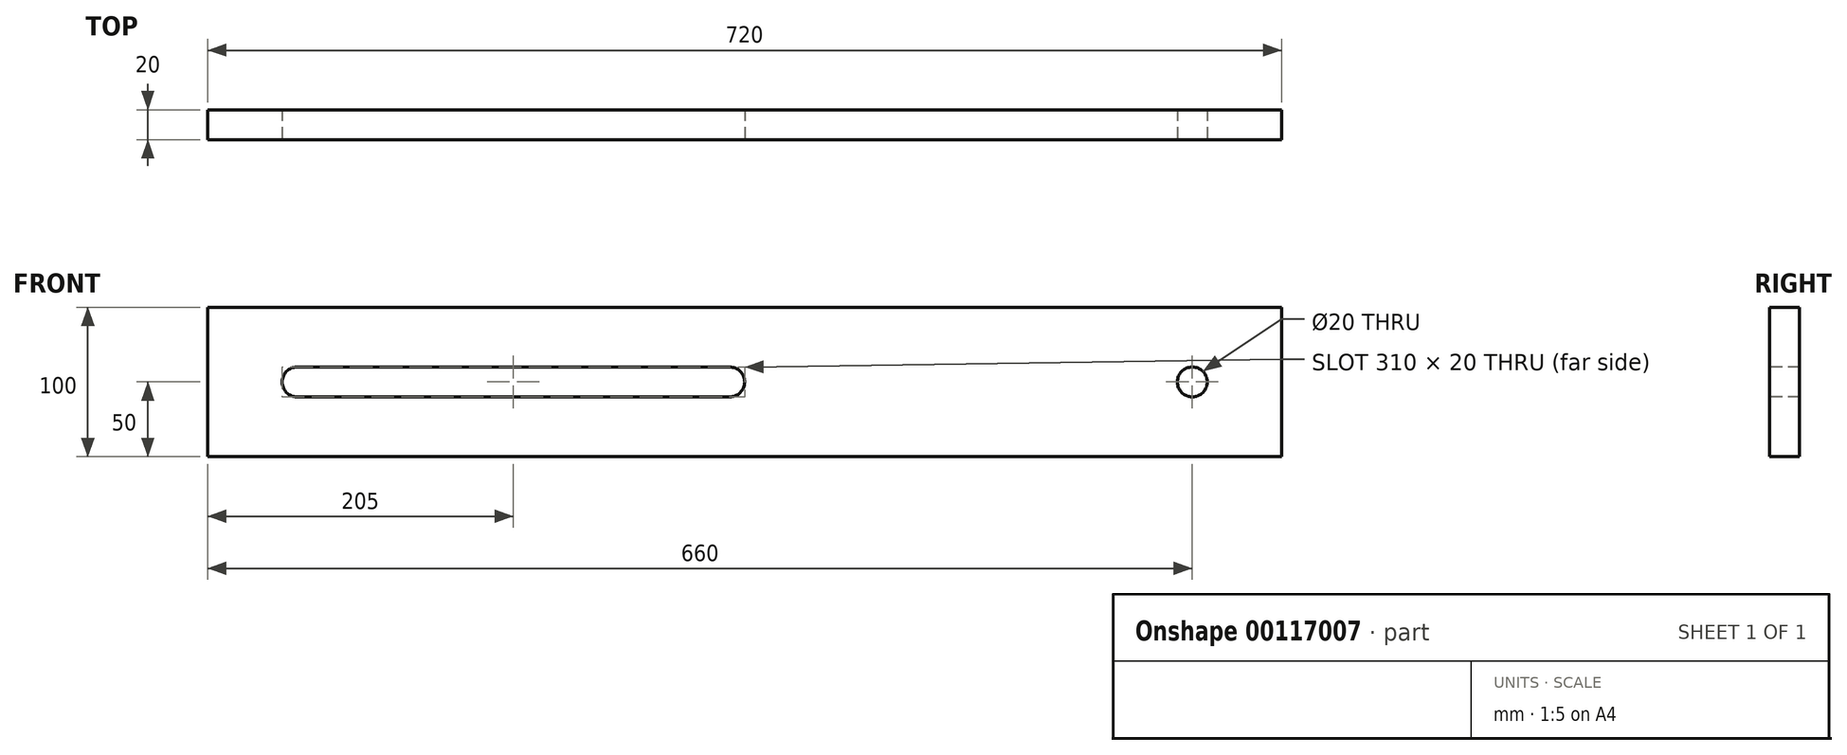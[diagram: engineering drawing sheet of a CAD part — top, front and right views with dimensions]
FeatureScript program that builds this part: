
annotation { "Feature Type Name" : "Feature", "Feature Type Description" : "" }
export const myFeature = defineFeature(function(context is Context, id is Id, definition is map)
    precondition{}
    {
        {
            var Q0;
            Q0=qCreatedBy(makeId("Top.planeOp"),FACE);
            var sketch = newSketch(context, id + "F0", { "sketchPlane" : qUnion([Q0])});
            skLineSegment(sketch, "E0.bottom", {"start": v(-359.02, 161.63) * mm, "end": v(360.98, 161.63) * mm});
            skLineSegment(sketch, "E0.top", {"start": v(-359.02, 141.63) * mm, "end": v(360.98, 141.63) * mm});
            skLineSegment(sketch, "E0.left", {"start": v(-359.02, 161.63) * mm, "end": v(-359.02, 141.63) * mm});
            skLineSegment(sketch, "E0.right", {"start": v(360.98, 161.63) * mm, "end": v(360.98, 141.63) * mm});
            skSolve(sketch);
        }
        {
            var Q0;
            Q0=makeQuery(id+"F0.imprint","IMPRINT",FACE,{"disambiguationData":[TD([[makeQuery(id+"F0.imprint","IMPRINT",EDGE,{"derivedFrom":sQuery(id+"F0.wireOp",EDGE,"E0.bottom")}),-1.0]])]});
            extrude(context, id + "F1", {"entities" : qUnion([Q0]), "depth" : 100 * mm, "offsetDistance" : 25 * mm});
        }
        {
            var Q0;
            Q0=makeQuery(id+"F1.opExtrude","SWEPT_FACE",FACE,{"disambiguationData":[OSD([sQuery(id+"F0.wireOp",EDGE,"E0.top")])]});
            var sketch = newSketch(context, id + "F2", { "sketchPlane" : qUnion([Q0])});
            skLineSegment(sketch, "E1.bottom", {"start": v(-309.02, 60) * mm, "end": v(-9.02, 60) * mm});
            skLineSegment(sketch, "E1.top", {"start": v(-309.02, 40) * mm, "end": v(-9.02, 40) * mm});
            skLineSegment(sketch, "E2", {"start": v(-309.02, 100) * mm, "end": v(-309.02, 60) * mm});
            skLineSegment(sketch, "E3.trimOffspring", {"start": v(-309.02, 40) * mm, "end": v(-309.02, 0) * mm});
            skArc(sketch, "E4", {"start": v(-299.02, 60) * mm, "mid": v(-309.02, 50) * mm, "end": v(-299.02, 40) * mm});
            skArc(sketch, "E5", {"start": v(-9.02, 40) * mm, "mid": v(0.98, 50) * mm, "end": v(-9.02, 60) * mm});
            skCircle(sketch, "E6", {"center": v(300.98, 50) * mm, "radius": 10 * mm});
            skSolve(sketch);
        }
        {
            var Q0;
            {var subQ2=sQuery(id+"F2.wireOp",EDGE,"E4");Q0=makeQuery(id+"F2.imprint","IMPRINT",FACE,{"disambiguationData":[TD([[makeQuery(id+"F2.imprint","IMPRINT",EDGE,{"derivedFrom":subQ2}),1.0]])]});}
            var Q1;
            Q1=makeQuery(id+"F2.imprint","IMPRINT",FACE,{"disambiguationData":[TD([[makeQuery(id+"F2.imprint","IMPRINT",EDGE,{"derivedFrom":sQuery(id+"F2.wireOp",EDGE,"E6")}),1.0]])]});
            extrude(context, id + "F3", {"entities" : qUnion([Q0, Q1]), "operationType" : NewBodyOperationType.REMOVE, "endBound" : BoundingType.THROUGH_ALL, "oppositeDirection" : true, "depth" : 25 * mm, "offsetDistance" : 25 * mm});
        }
    });
